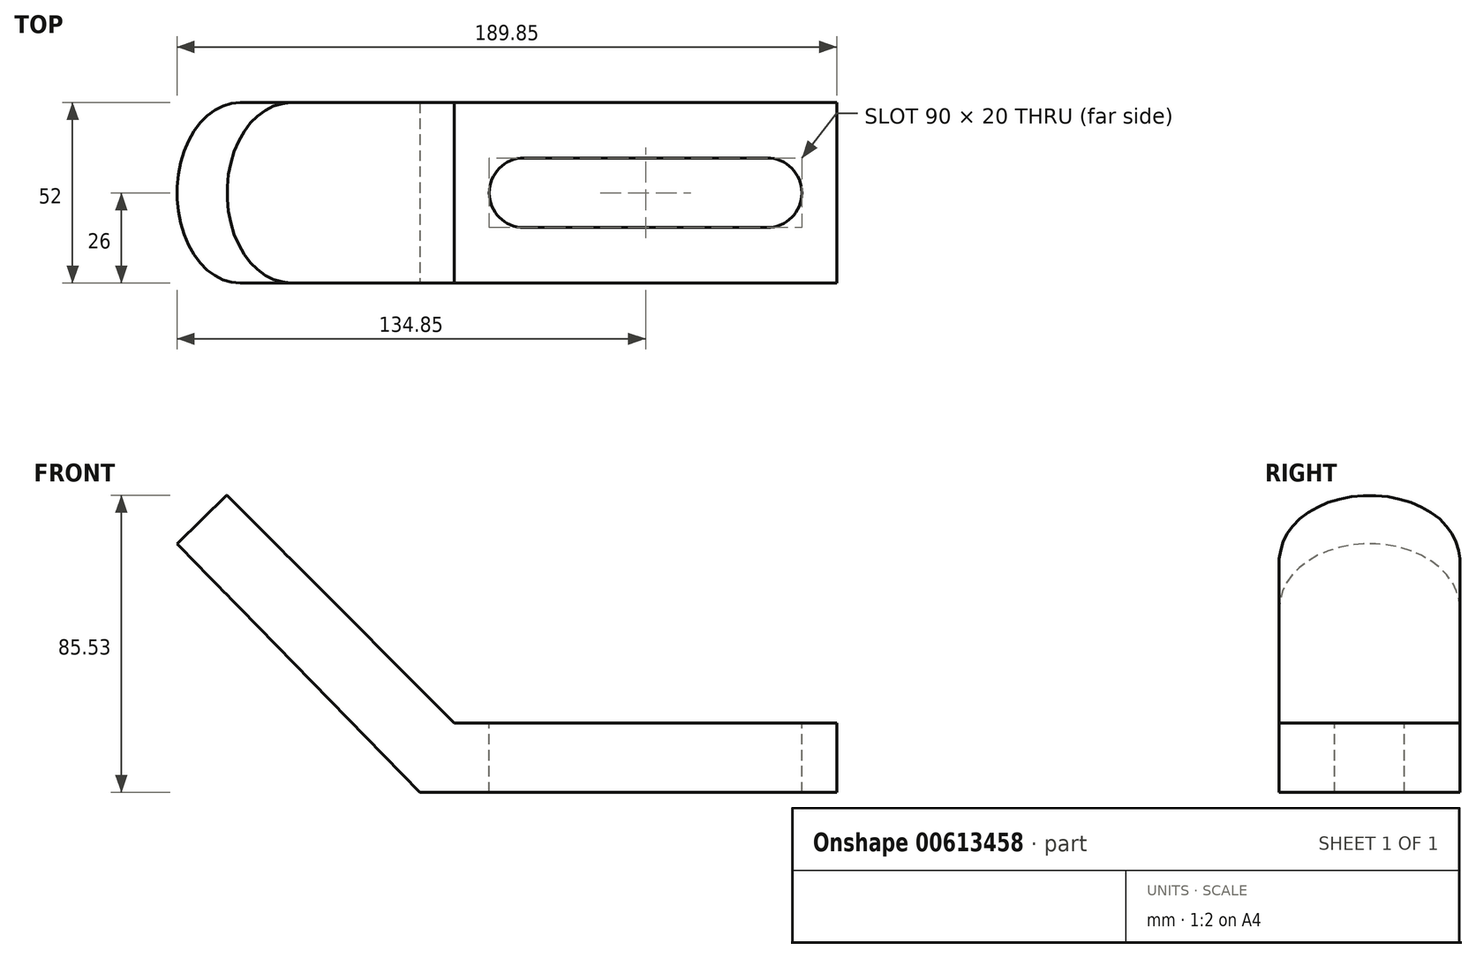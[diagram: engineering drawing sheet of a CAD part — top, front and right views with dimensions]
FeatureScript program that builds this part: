
annotation { "Feature Type Name" : "Feature", "Feature Type Description" : "" }
export const myFeature = defineFeature(function(context is Context, id is Id, definition is map)
    precondition{}
    {
        {
            var Q0;
            Q0=qCreatedBy(makeId("Front.planeOp"),FACE);
            var sketch = newSketch(context, id + "F0", { "sketchPlane" : qUnion([Q0])});
            skLineSegment(sketch, "E0", {"start": v(0, 0) * mm, "end": v(120, 0) * mm});
            skLineSegment(sketch, "E1", {"start": v(120, 0) * mm, "end": v(120, 20) * mm});
            skLineSegment(sketch, "E2", {"start": v(120, 20) * mm, "end": v(10, 20) * mm});
            skLineSegment(sketch, "E3", {"start": v(0, 0) * mm, "end": v(-69.85, 71.56) * mm});
            skLineSegment(sketch, "E4", {"start": v(-69.85, 71.56) * mm, "end": v(-55.53, 85.53) * mm});
            skLineSegment(sketch, "E5", {"start": v(-55.53, 85.53) * mm, "end": v(10, 20) * mm});
            skSolve(sketch);
        }
        {
            var Q0;
            Q0=makeQuery(id+"F0.imprint","IMPRINT",FACE,{"disambiguationData":[TD([[makeQuery(id+"F0.imprint","IMPRINT",EDGE,{"derivedFrom":sQuery(id+"F0.wireOp",EDGE,"E0")}),1.0]])]});
            extrude(context, id + "F1", {"entities" : qUnion([Q0]), "oppositeDirection" : true, "depth" : 52 * mm, "offsetDistance" : 25 * mm});
        }
        {
            var Q0;
            Q0=makeQuery(id+"F1.opExtrude","SWEPT_FACE",FACE,{"disambiguationData":[OSD([sQuery(id+"F0.wireOp",EDGE,"E5")])]});
            var sketch = newSketch(context, id + "F2", { "sketchPlane" : qUnion([Q0])});
            skCircle(sketch, "E6", {"center": v(-73.75, 26) * mm, "radius": 10 * mm});
            skSolve(sketch);
        }
        {
            var Q0;
            Q0=makeQuery(id+"F2.imprint","IMPRINT",FACE,{"disambiguationData":[TD([[makeQuery(id+"F2.imprint","IMPRINT",EDGE,{"derivedFrom":sQuery(id+"F2.wireOp",EDGE,"E6")}),1.0]])]});
            extrude(context, id + "F3", {"entities" : qUnion([Q0]), "operationType" : NewBodyOperationType.REMOVE, "oppositeDirection" : true, "depth" : 21 * mm, "offsetDistance" : 25 * mm});
        }
        {
            var Q0;
            Q0=makeQuery(id+"F1.opExtrude","SWEPT_FACE",FACE,{"disambiguationData":[OSD([sQuery(id+"F0.wireOp",EDGE,"E2")])]});
            var sketch = newSketch(context, id + "F4", { "sketchPlane" : qUnion([Q0])});
            skLineSegment(sketch, "E7", {"start": v(30, 16) * mm, "end": v(100, 16) * mm});
            skLineSegment(sketch, "E8", {"start": v(110, 26) * mm, "end": v(110, 26) * mm});
            skLineSegment(sketch, "E9", {"start": v(100, 36) * mm, "end": v(30, 36) * mm});
            skLineSegment(sketch, "E10", {"start": v(20, 26) * mm, "end": v(20, 26) * mm});
            skPoint(sketch, "E11.visualSharp", {"position": v(110, 36) * mm});
            skArc(sketch, "E11.filletArc", {"start": v(110, 26) * mm, "mid": v(107.07, 33.07) * mm, "end": v(100, 36) * mm});
            skPoint(sketch, "E12.visualSharp", {"position": v(110, 16) * mm});
            skArc(sketch, "E12.filletArc", {"start": v(100, 16) * mm, "mid": v(107.07, 18.93) * mm, "end": v(110, 26) * mm});
            skPoint(sketch, "E13.visualSharp", {"position": v(20, 16) * mm});
            skArc(sketch, "E13.filletArc", {"start": v(20, 26) * mm, "mid": v(22.93, 18.93) * mm, "end": v(30, 16) * mm});
            skPoint(sketch, "E14.visualSharp", {"position": v(20, 36) * mm});
            skArc(sketch, "E14.filletArc", {"start": v(30, 36) * mm, "mid": v(22.93, 33.07) * mm, "end": v(20, 26) * mm});
            skSolve(sketch);
        }
        {
            var Q0;
            Q0=makeQuery(id+"F4.imprint","IMPRINT",FACE,{"disambiguationData":[TD([[makeQuery(id+"F4.imprint","IMPRINT",EDGE,{"derivedFrom":sQuery(id+"F4.wireOp",EDGE,"E7")}),1.0]])]});
            extrude(context, id + "F5", {"entities" : qUnion([Q0]), "operationType" : NewBodyOperationType.REMOVE, "oppositeDirection" : true, "depth" : 21 * mm, "offsetDistance" : 25 * mm});
        }
        {
            var Q0;
            Q0=makeQuery(id+"F1.opExtrude","CAP_EDGE",EDGE,{"disambiguationData":[OSD([sQuery(id+"F0.wireOp",EDGE,"E4")])],"isStart":true});
            var Q1;
            Q1=makeQuery(id+"F1.opExtrude","CAP_EDGE",EDGE,{"disambiguationData":[OSD([sQuery(id+"F0.wireOp",EDGE,"E4")])],"isStart":false});
            fillet(context, id + "F6", {"entities" : qUnion([Q0, Q1]), "radius" : 26 * mm, "tangentPropagation" : true, "allowEdgeOverflow" : false});
        }
    });
